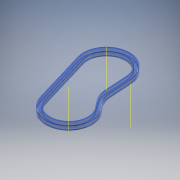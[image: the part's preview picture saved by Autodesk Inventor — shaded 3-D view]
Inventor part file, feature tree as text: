
AUTODESK INVENTOR PART (.ipt)
format: ipt  version: 2017 (Build 210142000, 142)  size: 227,328 bytes
history: native  units: mm
features: other x6, plane x2, pattern_linear x1
ambient origin geometry x8: Origin, YZ Plane, XZ Plane, XY Plane, X Axis, Y Axis, Z Axis, Center Point
bodies: Solid1 (feature_tree), Solid (feature_tree)
feature tree (9):
  other  "Work Axis1"
  other  "Work Axis2"
  other  "Work Axis3"
  plane  "Work Plane2"
  plane  "Work Plane3"
  other  "Path"
  other  "Section Plane"
  pattern_linear  "Strand Pattern"  Spacing1=0.0mm  [1 undecoded]
  other  "Section Sketch"
note: 1 required parameter value undecoded (feature->parameter linkage not recoverable at this tier; creation-order binding heuristic only, values carry confidence <= 0.55)
